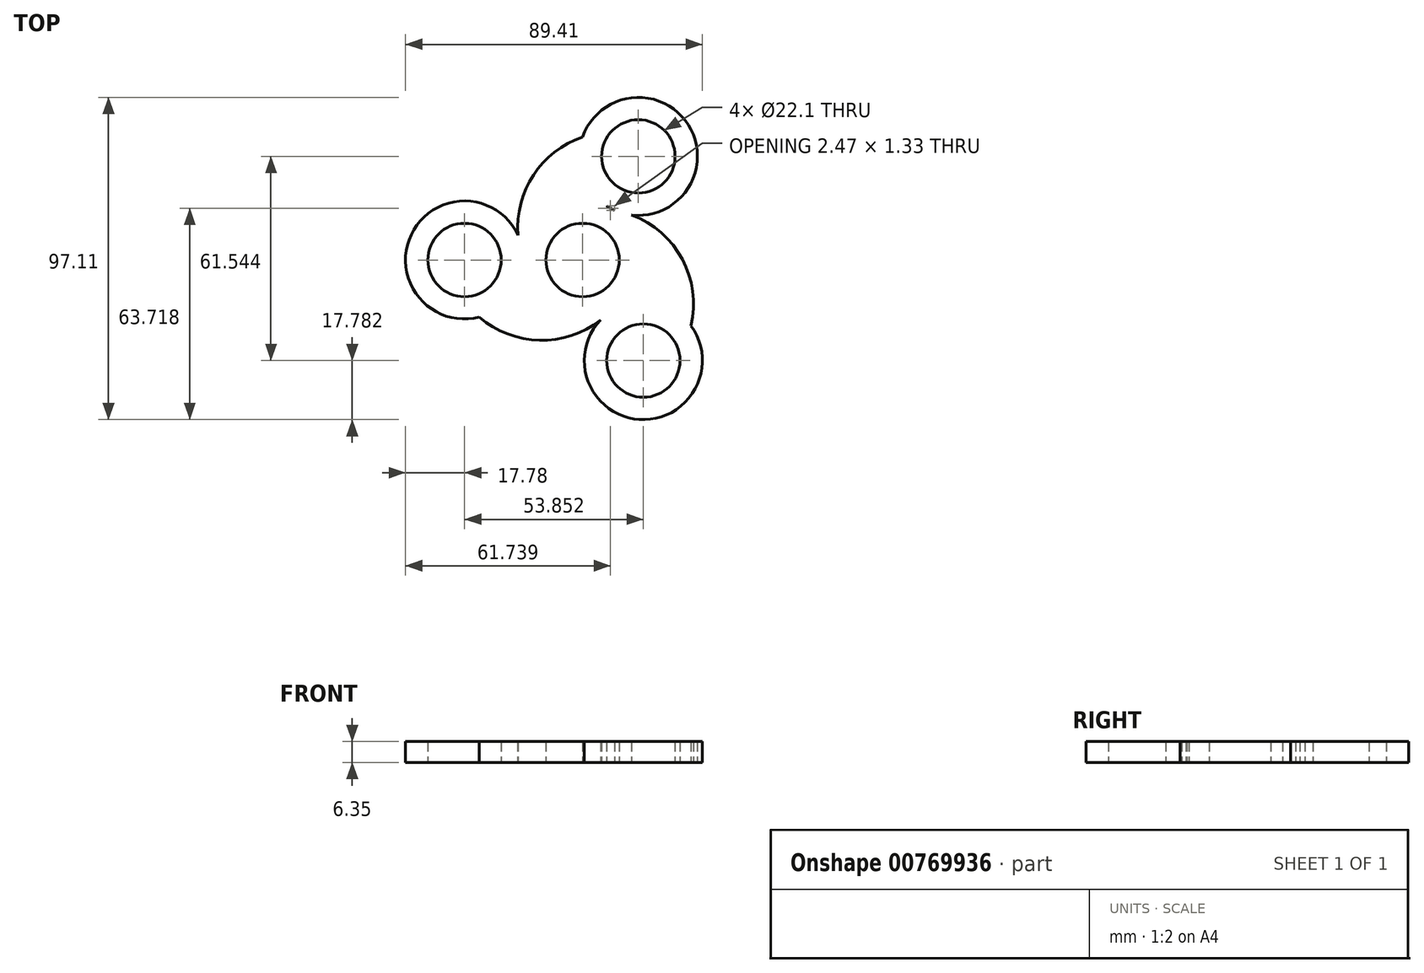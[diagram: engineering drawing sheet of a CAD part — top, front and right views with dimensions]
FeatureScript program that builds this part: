
annotation { "Feature Type Name" : "Feature", "Feature Type Description" : "" }
export const myFeature = defineFeature(function(context is Context, id is Id, definition is map)
    precondition{}
    {
        {
            var Q0;
            Q0=qCreatedBy(makeId("Top.planeOp"),FACE);
            var sketch = newSketch(context, id + "F0", { "sketchPlane" : qUnion([Q0])});
            skCircle(sketch, "E0", {"center": v(0, 0) * mm, "radius": 11.05 * mm});
            skCircle(sketch, "E1", {"center": v(0, 0) * mm, "radius": 17.78 * mm});
            skLineSegment(sketch, "E2", {"start": v(-17.78, 0) * mm, "end": v(-35.56, 0) * mm});
            skCircle(sketch, "E3", {"center": v(-35.56, 0) * mm, "radius": 11.05 * mm});
            skLineSegment(sketch, "E4", {"start": v(9.63, 14.94) * mm, "end": v(16.8, 31.22) * mm});
            skLineSegment(sketch, "E5", {"start": v(7.78, -15.99) * mm, "end": v(18.3, -30.33) * mm});
            skCircle(sketch, "E6", {"center": v(16.8, 31.22) * mm, "radius": 11.05 * mm});
            skCircle(sketch, "E7", {"center": v(18.3, -30.33) * mm, "radius": 11.05 * mm});
            skCircle(sketch, "E8", {"center": v(16.8, 31.22) * mm, "radius": 17.78 * mm});
            skCircle(sketch, "E9", {"center": v(18.3, -30.33) * mm, "radius": 17.78 * mm});
            skCircle(sketch, "E10", {"center": v(-35.56, 0) * mm, "radius": 17.78 * mm});
            skArc(sketch, "E11", {"start": v(0, 37.04) * mm, "mid": v(-16.7, 22.27) * mm, "end": v(-17.78, 0) * mm});
            skArc(sketch, "E12", {"start": v(-31.12, -17.22) * mm, "mid": v(-11.43, -24.2) * mm, "end": v(7.78, -15.99) * mm});
            skArc(sketch, "E13", {"start": v(32.67, -19.87) * mm, "mid": v(28.66, 2.5) * mm, "end": v(9.63, 14.94) * mm});
            skSolve(sketch);
        }
        {
            var Q0;
            Q0=makeQuery(id+"F0.imprint","IMPRINT",FACE,{"disambiguationData":[TD([[makeQuery(id+"F0.imprint","IMPRINT",EDGE,{"derivedFrom":sQuery(id+"F0.wireOp",EDGE,"E0")}),-1.0]])]});
            var Q1;
            {var subQ3=sQuery(id+"F0.wireOp",EDGE,"E9");var subQ5=sQuery(id+"F0.wireOp",EDGE,"E12");var subQ6=makeQuery(id+"F0.imprint","INTERSECT",VERTEX,{"derivedFrom":[subQ3,subQ5]});Q1=makeQuery(id+"F0.imprint","IMPRINT",FACE,{"disambiguationData":[TD([[makeQuery(id+"F0.imprint","IMPRINT",EDGE,{"disambiguationData":[TD([[subQ6,1.0]])],"derivedFrom":subQ3}),-1.0]])]});}
            var Q2;
            Q2=makeQuery(id+"F0.imprint","IMPRINT",FACE,{"disambiguationData":[TD([[makeQuery(id+"F0.imprint","IMPRINT",EDGE,{"derivedFrom":sQuery(id+"F0.wireOp",EDGE,"E3")}),-1.0]])]});
            var Q3;
            {var subQ0=sQuery(id+"F0.wireOp",EDGE,"E11");var subQ4=sQuery(id+"F0.wireOp",EDGE,"E8");var subQ7=makeQuery(id+"F0.imprint","INTERSECT",VERTEX,{"derivedFrom":[subQ4,subQ0]});Q3=makeQuery(id+"F0.imprint","IMPRINT",FACE,{"disambiguationData":[TD([[makeQuery(id+"F0.imprint","IMPRINT",EDGE,{"disambiguationData":[TD([[subQ7,-1.0]])],"derivedFrom":subQ4}),-1.0]])]});}
            var Q4;
            {var subQ0=sQuery(id+"F0.wireOp",EDGE,"E11");var subQ1=sQuery(id+"F0.wireOp",EDGE,"E10");var subQ3=makeQuery(id+"F0.imprint","INTERSECT",VERTEX,{"derivedFrom":[subQ1,subQ0]});Q4=makeQuery(id+"F0.imprint","IMPRINT",FACE,{"disambiguationData":[TD([[makeQuery(id+"F0.imprint","IMPRINT",EDGE,{"disambiguationData":[TD([[subQ3,1.0]])],"derivedFrom":subQ1}),1.0]])]});}
            var Q5;
            Q5=makeQuery(id+"F0.imprint","IMPRINT",FACE,{"disambiguationData":[TD([[makeQuery(id+"F0.imprint","IMPRINT",EDGE,{"derivedFrom":sQuery(id+"F0.wireOp",EDGE,"E6")}),-1.0]])]});
            var Q6;
            {var subQ0=sQuery(id+"F0.wireOp",EDGE,"E1");var subQ1=makeQuery(id+"F0.imprint","INTERSECT",VERTEX,{"derivedFrom":[subQ0,sQuery(id+"F0.wireOp",EDGE,"E13")]});Q6=makeQuery(id+"F0.imprint","IMPRINT",FACE,{"disambiguationData":[TD([[makeQuery(id+"F0.imprint","IMPRINT",EDGE,{"disambiguationData":[TD([[subQ1,1.0]])],"derivedFrom":subQ0}),1.0]])]});}
            var Q7;
            {var subQ0=sQuery(id+"F0.wireOp",EDGE,"E13");var subQ1=sQuery(id+"F0.wireOp",EDGE,"E1");var subQ2=makeQuery(id+"F0.imprint","INTERSECT",VERTEX,{"derivedFrom":[subQ1,subQ0]});Q7=makeQuery(id+"F0.imprint","IMPRINT",FACE,{"disambiguationData":[TD([[makeQuery(id+"F0.imprint","IMPRINT",EDGE,{"disambiguationData":[TD([[subQ2,1.0]])],"derivedFrom":subQ1}),-1.0]])]});}
            var Q8;
            {var subQ3=sQuery(id+"F0.wireOp",EDGE,"E8");var subQ5=sQuery(id+"F0.wireOp",EDGE,"E13");var subQ6=makeQuery(id+"F0.imprint","INTERSECT",VERTEX,{"derivedFrom":[subQ3,subQ5]});Q8=makeQuery(id+"F0.imprint","IMPRINT",FACE,{"disambiguationData":[TD([[makeQuery(id+"F0.imprint","IMPRINT",EDGE,{"disambiguationData":[TD([[subQ6,1.0]])],"derivedFrom":subQ3}),-1.0]])]});}
            var Q9;
            {var subQ0=sQuery(id+"F0.wireOp",EDGE,"E12");var subQ1=sQuery(id+"F0.wireOp",EDGE,"E9");var subQ3=makeQuery(id+"F0.imprint","INTERSECT",VERTEX,{"derivedFrom":[subQ1,subQ0]});Q9=makeQuery(id+"F0.imprint","IMPRINT",FACE,{"disambiguationData":[TD([[makeQuery(id+"F0.imprint","IMPRINT",EDGE,{"disambiguationData":[TD([[subQ3,1.0]])],"derivedFrom":subQ1}),1.0]])]});}
            var Q10;
            Q10=makeQuery(id+"F0.imprint","IMPRINT",FACE,{"disambiguationData":[TD([[makeQuery(id+"F0.imprint","IMPRINT",EDGE,{"derivedFrom":sQuery(id+"F0.wireOp",EDGE,"E7")}),-1.0]])]});
            var Q11;
            {var subQ0=sQuery(id+"F0.wireOp",EDGE,"E9");var subQ1=sQuery(id+"F0.wireOp",EDGE,"E1");var subQ3=makeQuery(id+"F0.imprint","INTERSECT",VERTEX,{"derivedFrom":[subQ1,subQ0]});Q11=makeQuery(id+"F0.imprint","IMPRINT",FACE,{"disambiguationData":[TD([[makeQuery(id+"F0.imprint","IMPRINT",EDGE,{"disambiguationData":[TD([[subQ3,1.0]])],"derivedFrom":subQ1}),1.0]])]});}
            var Q12;
            {var subQ0=sQuery(id+"F0.wireOp",EDGE,"E13");var subQ1=sQuery(id+"F0.wireOp",EDGE,"E8");var subQ2=makeQuery(id+"F0.imprint","INTERSECT",VERTEX,{"disambiguationData":[OD(0.0)],"derivedFrom":[subQ1,subQ0]});Q12=makeQuery(id+"F0.imprint","IMPRINT",FACE,{"disambiguationData":[TD([[makeQuery(id+"F0.imprint","IMPRINT",EDGE,{"disambiguationData":[TD([[subQ2,1.0]])],"derivedFrom":subQ1}),1.0]])]});}
            extrude(context, id + "F1", {"entities" : qUnion([Q0, Q1, Q2, Q3, Q4, Q5, Q6, Q7, Q8, Q9, Q10, Q11, Q12]), "depth" : 6.35 * mm, "offsetDistance" : 25.4 * mm});
        }
    });
